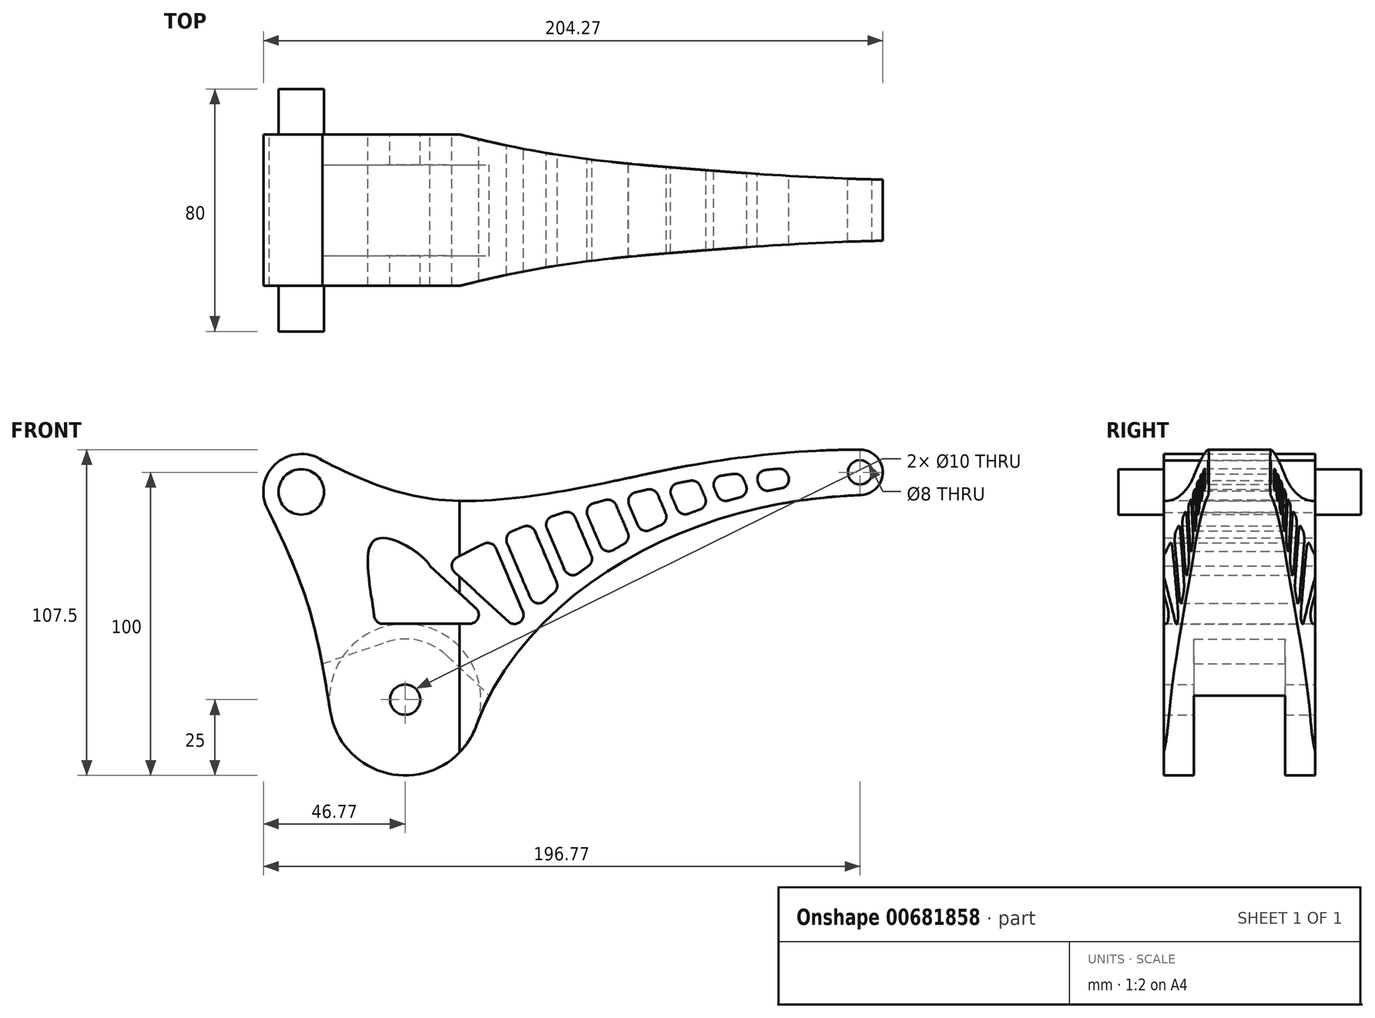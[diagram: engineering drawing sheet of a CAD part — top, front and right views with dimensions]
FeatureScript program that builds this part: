
annotation { "Feature Type Name" : "Feature", "Feature Type Description" : "" }
export const myFeature = defineFeature(function(context is Context, id is Id, definition is map)
    precondition{}
    {
        {
            var Q0;
            Q0=qCreatedBy(makeId("Front.planeOp"),FACE);
            var sketch = newSketch(context, id + "F0", { "sketchPlane" : qUnion([Q0])});
            skCircle(sketch, "E0", {"center": v(-150, 0) * mm, "radius": 25 * mm});
            skLineSegment(sketch, "E1", {"start": v(-150, 0) * mm, "end": v(0, 0) * mm, "construction": true});
            skLineSegment(sketch, "E2", {"start": v(0, 0) * mm, "end": v(0, 75) * mm, "construction": true});
            skCircle(sketch, "E3", {"center": v(0, 75) * mm, "radius": 7.5 * mm});
            skFitSpline(sketch, "E4", {"points": [v(-126.41, -8.3) * mm, v(0.28, 67.5) * mm], "startDerivative": vector(37.45, 106.54) * mm, "endDerivative": vector(204.08, 7.67) * mm});
            skFitSpline(sketch, "E5", {"points": [v(-174.65, -4.18) * mm, v(0, 82.5) * mm], "startDerivative": vector(-27.01, 159.38) * mm, "endDerivative": vector(228.63, 0) * mm});
            skCircle(sketch, "E6", {"center": v(-150, 0) * mm, "radius": 5 * mm});
            skCircle(sketch, "E7", {"center": v(0, 75) * mm, "radius": 4 * mm});
            skLineSegment(sketch, "E8", {"start": v(-157.26, 25) * mm, "end": v(-128.76, 25.02) * mm});
            skLineSegment(sketch, "E9", {"start": v(-126.73, 30.23) * mm, "end": v(-147.98, 49.75) * mm});
            skFitSpline(sketch, "E10", {"points": [v(-161.56, 25) * mm, v(-161.04, 51.72) * mm, v(-141.86, 44.13) * mm], "startDerivative": vector(25.87, -24.1) * mm, "endDerivative": vector(10.56, -24.04) * mm});
            skLineSegment(sketch, "E11", {"start": v(-133.63, 42) * mm, "end": v(-115.96, 25.77) * mm});
            skLineSegment(sketch, "E12", {"start": v(-111.17, 29.16) * mm, "end": v(-120, 49.89) * mm});
            skLineSegment(sketch, "E13", {"start": v(-116.39, 51.6) * mm, "end": v(-108.72, 33.6) * mm});
            skLineSegment(sketch, "E14", {"start": v(-93.93, 60.12) * mm, "end": v(-88.62, 47.65) * mm});
            skLineSegment(sketch, "E15", {"start": v(-85.6, 50.79) * mm, "end": v(-89.84, 60.71) * mm});
            skLineSegment(sketch, "E16", {"start": v(-107.17, 55.47) * mm, "end": v(-100.06, 38.8) * mm});
            skLineSegment(sketch, "E17", {"start": v(-103.25, 56.5) * mm, "end": v(-97.46, 42.9) * mm});
            skFitSpline(sketch, "E18", {"points": [v(-136.72, 44.83) * mm, v(-121.23, 52.77) * mm], "startDerivative": vector(16, 8.91) * mm, "endDerivative": vector(16.2, 7.62) * mm});
            skFitSpline(sketch, "E19", {"points": [v(-117.57, 54.38) * mm, v(-108.29, 58.1) * mm], "startDerivative": vector(11.62, 4.84) * mm, "endDerivative": vector(9.7, 3.4) * mm});
            skFitSpline(sketch, "E20", {"points": [v(-104.53, 59.48) * mm, v(-95.02, 62.67) * mm], "startDerivative": vector(9.5, 3.2) * mm, "endDerivative": vector(9.5, 3.2) * mm});
            skFitSpline(sketch, "E21", {"points": [v(-107.07, 29.72) * mm, v(-99.22, 36.83) * mm], "startDerivative": vector(7.84, 7.1) * mm, "endDerivative": vector(7.84, 7.1) * mm});
            skFitSpline(sketch, "E22", {"points": [v(-95.99, 39.44) * mm, v(-87.68, 45.45) * mm], "startDerivative": vector(8.3, 6.01) * mm, "endDerivative": vector(8.3, 6.01) * mm});
            skLineSegment(sketch, "E23", {"start": v(-80.43, 64.16) * mm, "end": v(-76.6, 55.17) * mm});
            skLineSegment(sketch, "E24", {"start": v(-76.15, 64.3) * mm, "end": v(-73.25, 57.5) * mm});
            skFitSpline(sketch, "E25", {"points": [v(-91.17, 63.85) * mm, v(-81.47, 66.58) * mm], "startDerivative": vector(9.7, 2.73) * mm, "endDerivative": vector(9.7, 2.73) * mm});
            skFitSpline(sketch, "E26", {"points": [v(-84.28, 47.66) * mm, v(-75.57, 52.73) * mm], "startDerivative": vector(8.7, 5.07) * mm, "endDerivative": vector(8.7, 5.07) * mm});
            skLineSegment(sketch, "E27", {"start": v(-66.67, 67.58) * mm, "end": v(-64.1, 61.53) * mm});
            skLineSegment(sketch, "E28", {"start": v(-62.22, 67.34) * mm, "end": v(-60.36, 62.97) * mm});
            skLineSegment(sketch, "E29", {"start": v(-52.68, 70.44) * mm, "end": v(-51.09, 66.71) * mm});
            skLineSegment(sketch, "E30", {"start": v(-48.04, 69.76) * mm, "end": v(-47.03, 67.39) * mm});
            skFitSpline(sketch, "E31", {"points": [v(-77.55, 67.6) * mm, v(-67.66, 69.9) * mm], "startDerivative": vector(9.89, 2.3) * mm, "endDerivative": vector(9.89, 2.3) * mm});
            skFitSpline(sketch, "E32", {"points": [v(-72, 54.59) * mm, v(-67.74, 56.66) * mm, v(-62.94, 58.8) * mm], "startDerivative": vector(8.6, 4.27) * mm, "endDerivative": vector(9.53, 4.17) * mm});
            skFitSpline(sketch, "E33", {"points": [v(-59.24, 60.33) * mm, v(-53.97, 62.32) * mm, v(-49.82, 63.74) * mm], "startDerivative": vector(10.29, 3.67) * mm, "endDerivative": vector(8.5, 3.15) * mm});
            skFitSpline(sketch, "E34", {"points": [v(-63.67, 70.74) * mm, v(-59.24, 71.62) * mm, v(-53.61, 72.64) * mm], "startDerivative": vector(9.14, 1.85) * mm, "endDerivative": vector(10.94, 1.96) * mm});
            skLineSegment(sketch, "E35", {"start": v(-37.62, 70.81) * mm, "end": v(-38.42, 72.7) * mm});
            skLineSegment(sketch, "E36", {"start": v(-33.24, 70.74) * mm, "end": v(-33.6, 71.6) * mm});
            skLineSegment(sketch, "E37", {"start": v(-23.91, 74.36) * mm, "end": v(-23.7, 73.86) * mm});
            skFitSpline(sketch, "E38", {"points": [v(-49.55, 73.32) * mm, v(-43.77, 74.2) * mm, v(-39.32, 74.82) * mm], "startDerivative": vector(11.26, 1.41) * mm, "endDerivative": vector(9.16, 1.58) * mm});
            skFitSpline(sketch, "E39", {"points": [v(-45.99, 64.95) * mm, v(-40.93, 66.4) * mm, v(-36.24, 67.59) * mm], "startDerivative": vector(10.07, 2.67) * mm, "endDerivative": vector(9.42, 2.6) * mm});
            skFitSpline(sketch, "E40", {"points": [v(-35.2, 75.33) * mm, v(-29, 76) * mm, v(-24.78, 76.4) * mm], "startDerivative": vector(11.9, 0.86) * mm, "endDerivative": vector(8.84, 1.29) * mm});
            skFitSpline(sketch, "E41", {"points": [v(-32.28, 68.5) * mm, v(-26.83, 69.57) * mm, v(-22.2, 70.36) * mm], "startDerivative": vector(10.69, 2.05) * mm, "endDerivative": vector(9.44, 1.68) * mm});
            skArc(sketch, "E42.filletArc", {"start": v(-133.02, 46.85) * mm, "mid": v(-134.58, 44.59) * mm, "end": v(-133.63, 42) * mm});
            skArc(sketch, "E43.filletArc", {"start": v(-120, 49.89) * mm, "mid": v(-121.71, 51.52) * mm, "end": v(-124.07, 51.41) * mm});
            skArc(sketch, "E44.filletArc", {"start": v(-114.79, 55.54) * mm, "mid": v(-116.4, 53.9) * mm, "end": v(-116.39, 51.6) * mm});
            skArc(sketch, "E45.filletArc", {"start": v(-107.17, 55.47) * mm, "mid": v(-108.76, 57.06) * mm, "end": v(-111.02, 57.09) * mm});
            skArc(sketch, "E46.filletArc", {"start": v(-101.45, 60.51) * mm, "mid": v(-103.23, 58.9) * mm, "end": v(-103.25, 56.5) * mm});
            skArc(sketch, "E47.filletArc", {"start": v(-93.93, 60.12) * mm, "mid": v(-95.46, 61.68) * mm, "end": v(-97.64, 61.79) * mm});
            skArc(sketch, "E48.filletArc", {"start": v(-87.89, 64.78) * mm, "mid": v(-89.78, 63.19) * mm, "end": v(-89.84, 60.71) * mm});
            skArc(sketch, "E49.filletArc", {"start": v(-80.43, 64.16) * mm, "mid": v(-81.9, 65.69) * mm, "end": v(-84, 65.87) * mm});
            skArc(sketch, "E50.filletArc", {"start": v(-74.07, 68.4) * mm, "mid": v(-76.06, 66.84) * mm, "end": v(-76.15, 64.3) * mm});
            skArc(sketch, "E51.filletArc", {"start": v(-66.67, 67.58) * mm, "mid": v(-68.08, 69.08) * mm, "end": v(-70.12, 69.33) * mm});
            skArc(sketch, "E52.filletArc", {"start": v(-60.04, 71.47) * mm, "mid": v(-62.11, 69.93) * mm, "end": v(-62.22, 67.34) * mm});
            skArc(sketch, "E53.filletArc", {"start": v(-52.68, 70.44) * mm, "mid": v(-54.01, 71.9) * mm, "end": v(-55.97, 72.22) * mm});
            skArc(sketch, "E54.filletArc", {"start": v(-45.76, 73.9) * mm, "mid": v(-47.9, 72.38) * mm, "end": v(-48.04, 69.76) * mm});
            skArc(sketch, "E55.filletArc", {"start": v(-38.42, 72.7) * mm, "mid": v(-39.68, 74.12) * mm, "end": v(-41.56, 74.5) * mm});
            skArc(sketch, "E56.filletArc", {"start": v(-31.2, 75.75) * mm, "mid": v(-33.44, 74.27) * mm, "end": v(-33.6, 71.6) * mm});
            skArc(sketch, "E57.filletArc", {"start": v(-33.24, 70.74) * mm, "mid": v(-31.87, 69.25) * mm, "end": v(-29.87, 68.97) * mm});
            skArc(sketch, "E58.filletArc", {"start": v(-39.65, 66.73) * mm, "mid": v(-37.7, 68.3) * mm, "end": v(-37.62, 70.81) * mm});
            skArc(sketch, "E59.filletArc", {"start": v(-47.03, 67.39) * mm, "mid": v(-45.55, 65.85) * mm, "end": v(-43.42, 65.68) * mm});
            skArc(sketch, "E60.filletArc", {"start": v(-52.89, 62.7) * mm, "mid": v(-51.1, 64.31) * mm, "end": v(-51.09, 66.71) * mm});
            skArc(sketch, "E61.filletArc", {"start": v(-60.36, 62.97) * mm, "mid": v(-58.77, 61.39) * mm, "end": v(-56.52, 61.35) * mm});
            skArc(sketch, "E62.filletArc", {"start": v(-65.63, 57.62) * mm, "mid": v(-64.06, 59.26) * mm, "end": v(-64.1, 61.53) * mm});
            skArc(sketch, "E63.filletArc", {"start": v(-73.25, 57.5) * mm, "mid": v(-71.54, 55.87) * mm, "end": v(-69.19, 55.97) * mm});
            skArc(sketch, "E64.filletArc", {"start": v(-77.85, 51.4) * mm, "mid": v(-76.52, 53.05) * mm, "end": v(-76.6, 55.17) * mm});
            skArc(sketch, "E65.filletArc", {"start": v(-85.6, 50.79) * mm, "mid": v(-83.8, 49.12) * mm, "end": v(-81.34, 49.37) * mm});
            skArc(sketch, "E66.filletArc", {"start": v(-89.62, 44.05) * mm, "mid": v(-88.49, 45.68) * mm, "end": v(-88.62, 47.65) * mm});
            skArc(sketch, "E67.filletArc", {"start": v(-97.46, 42.9) * mm, "mid": v(-95.5, 41.18) * mm, "end": v(-92.94, 41.64) * mm});
            skArc(sketch, "E68.filletArc", {"start": v(-100.8, 35.4) * mm, "mid": v(-99.9, 36.97) * mm, "end": v(-100.06, 38.8) * mm});
            skArc(sketch, "E69.filletArc", {"start": v(-108.72, 33.6) * mm, "mid": v(-106.6, 31.84) * mm, "end": v(-103.94, 32.55) * mm});
            skPoint(sketch, "E70.visualSharp", {"position": v(-105.73, 16.37) * mm});
            skArc(sketch, "E70.filletArc", {"start": v(-115.96, 25.77) * mm, "mid": v(-112.2, 25.53) * mm, "end": v(-111.17, 29.16) * mm});
            skPoint(sketch, "E71.visualSharp", {"position": v(-121.07, 25.03) * mm});
            skArc(sketch, "E71.filletArc", {"start": v(-128.76, 25.02) * mm, "mid": v(-125.96, 26.93) * mm, "end": v(-126.73, 30.23) * mm});
            skArc(sketch, "E72.filletArc", {"start": v(-160.25, 27.7) * mm, "mid": v(-159.27, 25.77) * mm, "end": v(-157.26, 25) * mm});
            skArc(sketch, "E73.filletArc", {"start": v(-147.98, 49.75) * mm, "mid": v(-148.2, 49.93) * mm, "end": v(-148.43, 50.1) * mm});
            skArc(sketch, "E74.filletArc", {"start": v(-23.91, 74.36) * mm, "mid": v(-25.11, 75.75) * mm, "end": v(-26.9, 76.18) * mm});
            skArc(sketch, "E75.filletArc", {"start": v(-25.95, 69.73) * mm, "mid": v(-23.82, 71.25) * mm, "end": v(-23.7, 73.86) * mm});
            skCircle(sketch, "E76", {"center": v(-150, 0) * mm, "radius": 17.5 * mm, "construction": true});
            skLineSegment(sketch, "E77.anchor1", {"start": v(-150, 0) * mm, "end": v(-163.36, 11.3) * mm, "construction": true});
            skLineSegment(sketch, "E77.anchor2", {"start": v(-150, 0) * mm, "end": v(-133.08, 4.47) * mm, "construction": true});
            skLineSegment(sketch, "E78", {"start": v(-150, 0) * mm, "end": v(0, 75) * mm, "construction": true});
            skLineSegment(sketch, "E79", {"start": v(-150, 0) * mm, "end": v(-184.27, 68.54) * mm, "construction": true});
            skCircle(sketch, "E80", {"center": v(-184.27, 68.54) * mm, "radius": 12.5 * mm});
            skFitSpline(sketch, "E81", {"points": [v(-196.1, 64.5) * mm, v(-182.23, 31.88) * mm, v(-174.65, -4.18) * mm], "startDerivative": vector(31.2, -64.5) * mm, "endDerivative": vector(11.75, -72.82) * mm});
            skFitSpline(sketch, "E82", {"points": [v(-180.08, 80.32) * mm, v(-139.18, 66.01) * mm, v(-65.78, 75.41) * mm], "startDerivative": vector(86.7, -43.7) * mm, "endDerivative": vector(139.63, 30.21) * mm});
            skLineSegment(sketch, "E83", {"start": v(-150, 0) * mm, "end": v(-150, 104.9) * mm, "construction": true});
            skCircle(sketch, "E84", {"center": v(-184.27, 68.54) * mm, "radius": 7.5 * mm});
            skFitSpline(sketch, "E85.trimOffspring", {"points": [v(-174.65, -4.18) * mm, v(0, 82.5) * mm], "startDerivative": vector(-27.01, 159.38) * mm, "endDerivative": vector(228.63, 0) * mm});
            skSolve(sketch);
        }
        {
            var Q0;
            Q0 = qSketchRegion(id + "F0", true);
            var Q1;
            Q1=makeQuery(id+"F0.imprint","IMPRINT",FACE,{"disambiguationData":[TD([[makeQuery(id+"F0.imprint","IMPRINT",EDGE,{"derivedFrom":sQuery(id+"F0.wireOp",EDGE,"E77.1.0")}),1.0]])]});
            var Q2;
            Q2=makeQuery(id+"F0.imprint","IMPRINT",FACE,{"disambiguationData":[TD([[makeQuery(id+"F0.imprint","IMPRINT",EDGE,{"derivedFrom":sQuery(id+"F0.wireOp",EDGE,"c3Ei9PqV-dirO-JtmI-PVfi-dcthlOHvN8EN")}),1.0]])]});
            var Q3;
            Q3=makeQuery(id+"F0.imprint","IMPRINT",FACE,{"disambiguationData":[TD([[makeQuery(id+"F0.imprint","IMPRINT",EDGE,{"derivedFrom":sQuery(id+"F0.wireOp",EDGE,"E77.2.0")}),1.0]])]});
            extrude(context, id + "F1", {"entities" : qUnion([Q0, Q1, Q2, Q3]), "endBound" : BoundingType.SYMMETRIC, "depth" : 50 * mm, "offsetDistance" : 25 * mm});
        }
        {
            var Q0;
            Q0=makeQuery(id+"F0.imprint","IMPRINT",FACE,{"disambiguationData":[TD([[makeQuery(id+"F0.imprint","IMPRINT",EDGE,{"derivedFrom":sQuery(id+"F0.wireOp",EDGE,"E84")}),1.0]])]});
            extrude(context, id + "F2", {"entities" : qUnion([Q0]), "operationType" : NewBodyOperationType.ADD, "endBound" : BoundingType.SYMMETRIC, "depth" : 80 * mm, "offsetDistance" : 25 * mm});
        }
        {
            var Q0;
            Q0=qCreatedBy(makeId("Top.planeOp"),FACE);
            var sketch = newSketch(context, id + "F3", { "sketchPlane" : qUnion([Q0])});
            skLineSegment(sketch, "E86", {"start": v(7.6, 25.1) * mm, "end": v(-132.4, 25.1) * mm});
            skLineSegment(sketch, "E87", {"start": v(7.6, 25.1) * mm, "end": v(7.6, 10.1) * mm});
            skFitSpline(sketch, "E88", {"points": [v(-132.4, 25.1) * mm, v(-60.92, 14.01) * mm, v(7.6, 10.1) * mm], "startDerivative": vector(167.87, -43.6) * mm, "endDerivative": vector(138.5, -2.36) * mm});
            skFitSpline(sketch, "E89.MirrorCS", {"points": [v(-132.4, -25.1) * mm, v(-60.92, -14.01) * mm, v(7.6, -10.1) * mm], "startDerivative": vector(167.87, 43.6) * mm, "endDerivative": vector(138.5, 2.36) * mm});
            skLineSegment(sketch, "E90.MirrorCS", {"start": v(7.6, -25.1) * mm, "end": v(7.6, -10.1) * mm});
            skLineSegment(sketch, "E91.MirrorCS", {"start": v(7.6, -25.1) * mm, "end": v(-132.4, -25.1) * mm});
            skSolve(sketch);
        }
        {
            var Q0;
            Q0 = qSketchRegion(id + "F3", true);
            extrude(context, id + "F4", {"entities" : qUnion([Q0]), "operationType" : NewBodyOperationType.REMOVE, "endBound" : BoundingType.SYMMETRIC, "oppositeDirection" : true, "depth" : 1000 * mm, "offsetDistance" : 25 * mm});
        }
        {
            var Q0;
            Q0=qCreatedBy(makeId("Front.planeOp"),FACE);
            var sketch = newSketch(context, id + "F5", { "sketchPlane" : qUnion([Q0])});
            skLineSegment(sketch, "E92", {"start": v(0, 0) * mm, "end": v(-150, 0) * mm, "construction": true});
            skLineSegment(sketch, "E93", {"start": v(-150, 0) * mm, "end": v(-150, 75) * mm, "construction": true});
            skCircle(sketch, "E94", {"center": v(-150, 0) * mm, "radius": 20 * mm});
            skLineSegment(sketch, "E95", {"start": v(-136.3, 14.57) * mm, "end": v(-92.53, -26.57) * mm});
            skLineSegment(sketch, "E96", {"start": v(-92.53, -26.57) * mm, "end": v(-290.53, -26.57) * mm});
            skLineSegment(sketch, "E97", {"start": v(-290.53, -26.57) * mm, "end": v(-156.43, 18.94) * mm});
            skSolve(sketch);
        }
        {
            var Q0;
            Q0 = qSketchRegion(id + "F5", true);
            extrude(context, id + "F6", {"entities" : qUnion([Q0]), "operationType" : NewBodyOperationType.REMOVE, "endBound" : BoundingType.SYMMETRIC, "depth" : 30 * mm, "offsetDistance" : 25 * mm});
        }
    });
